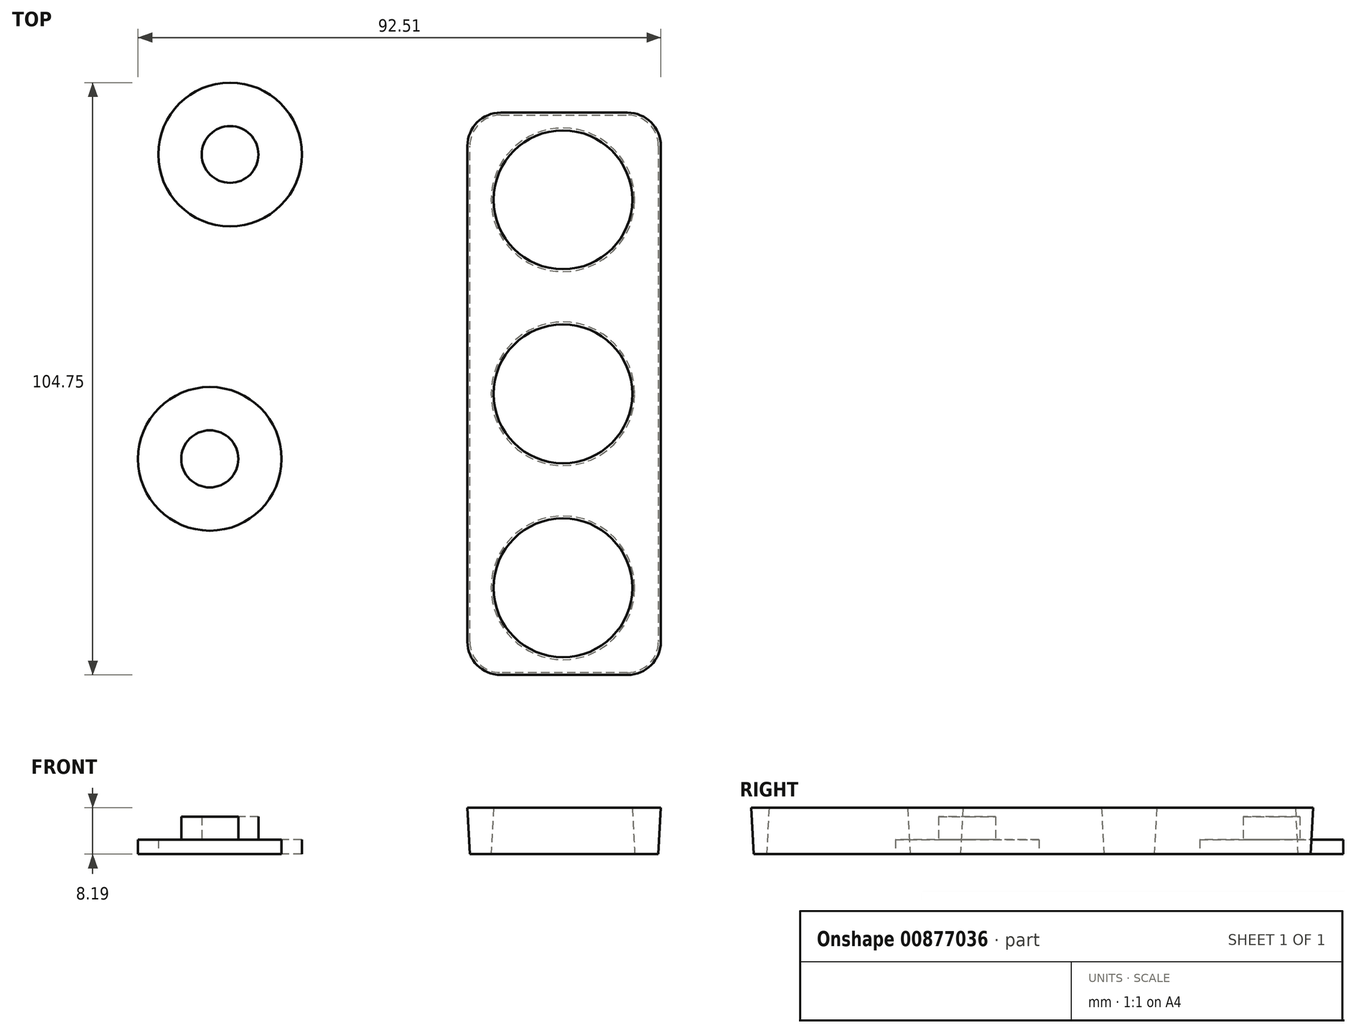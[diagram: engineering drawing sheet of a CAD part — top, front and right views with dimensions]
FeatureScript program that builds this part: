
annotation { "Feature Type Name" : "Feature", "Feature Type Description" : "" }
export const myFeature = defineFeature(function(context is Context, id is Id, definition is map)
    precondition{}
    {
        {
            var Q0;
            Q0=qCreatedBy(makeId("Top.planeOp"),FACE);
            var sketch = newSketch(context, id + "F0", { "sketchPlane" : qUnion([Q0])});
            skCircle(sketch, "E0", {"center": v(0, 0) * mm, "radius": 12.7 * mm});
            skCircle(sketch, "E1", {"center": v(0, 34.3) * mm, "radius": 12.7 * mm});
            skCircle(sketch, "E2.MirrorC", {"center": v(0, -34.3) * mm, "radius": 12.7 * mm});
            skLineSegment(sketch, "E3", {"start": v(-16.47, 21.22) * mm, "end": v(-16.47, -21.22) * mm});
            skLineSegment(sketch, "E4", {"start": v(16.89, 21.22) * mm, "end": v(16.89, -21.22) * mm});
            skLineSegment(sketch, "E5.MirrorCS", {"start": v(-16.47, -21.22) * mm, "end": v(-16.47, 21.22) * mm});
            skLineSegment(sketch, "E6.MirrorCS", {"start": v(16.89, -21.22) * mm, "end": v(16.89, 21.22) * mm});
            skLineSegment(sketch, "E7", {"start": v(-16.47, 21.22) * mm, "end": v(-16.47, 43.83) * mm});
            skLineSegment(sketch, "E8", {"start": v(16.89, 21.22) * mm, "end": v(16.89, 43.83) * mm});
            skLineSegment(sketch, "E9", {"start": v(11.43, 49.3) * mm, "end": v(-11, 49.3) * mm});
            skLineSegment(sketch, "E10", {"start": v(-16.47, -21.22) * mm, "end": v(-16.47, -43.83) * mm});
            skLineSegment(sketch, "E11", {"start": v(-11, -49.3) * mm, "end": v(11.43, -49.3) * mm});
            skLineSegment(sketch, "E12", {"start": v(16.89, -43.83) * mm, "end": v(16.89, -21.22) * mm});
            skPoint(sketch, "E13.visualSharp", {"position": v(-16.47, 49.3) * mm});
            skArc(sketch, "E13.filletArc", {"start": v(-11, 49.3) * mm, "mid": v(-14.87, 47.7) * mm, "end": v(-16.47, 43.83) * mm});
            skPoint(sketch, "E14.visualSharp", {"position": v(16.89, 49.3) * mm});
            skArc(sketch, "E14.filletArc", {"start": v(16.89, 43.83) * mm, "mid": v(15.29, 47.7) * mm, "end": v(11.43, 49.3) * mm});
            skPoint(sketch, "E15.visualSharp", {"position": v(-16.47, -49.3) * mm});
            skArc(sketch, "E15.filletArc", {"start": v(-16.47, -43.83) * mm, "mid": v(-14.87, -47.7) * mm, "end": v(-11, -49.3) * mm});
            skPoint(sketch, "E16.visualSharp", {"position": v(16.89, -49.3) * mm});
            skArc(sketch, "E16.filletArc", {"start": v(11.43, -49.3) * mm, "mid": v(15.29, -47.7) * mm, "end": v(16.89, -43.83) * mm});
            skSolve(sketch);
        }
        {
            var Q0;
            Q0=makeQuery(id+"F0.imprint","IMPRINT",FACE,{"disambiguationData":[TD([[makeQuery(id+"F0.imprint","IMPRINT",EDGE,{"derivedFrom":sQuery(id+"F0.wireOp",EDGE,"E1")}),-1.0]])]});
            extrude(context, id + "F1", {"entities" : qUnion([Q0]), "depth" : 8.2 * mm, "offsetDistance" : 25.4 * mm, "hasDraft" : true, "draftAngle" : 3 * degree});
        }
        {
            var Q0;
            Q0=qCreatedBy(makeId("Top.planeOp"),FACE);
            var sketch = newSketch(context, id + "F2", { "sketchPlane" : qUnion([Q0])});
            skCircle(sketch, "E17", {"center": v(-62.49, -11.5) * mm, "radius": 12.7 * mm});
            skCircle(sketch, "E18", {"center": v(-58.9, 42.33) * mm, "radius": 12.7 * mm});
            skSolve(sketch);
        }
        {
            var Q0;
            Q0 = qSketchRegion(id + "F2", true);
            extrude(context, id + "F3", {"entities" : qUnion([Q0]), "depth" : 2.54 * mm, "offsetDistance" : 25.4 * mm});
        }
        {
            var Q0;
            Q0=makeQuery(id+"F3.opExtrude","CAP_FACE",FACE,{"disambiguationData":[OSD([sQuery(id+"F2.wireOp",EDGE,"E17")])],"isStart":false});
            var sketch = newSketch(context, id + "F4", { "sketchPlane" : qUnion([Q0])});
            skCircle(sketch, "E19", {"center": v(-62.49, -11.5) * mm, "radius": 5.05 * mm});
            skSolve(sketch);
        }
        {
            var Q0;
            Q0 = qSketchRegion(id + "F4", true);
            extrude(context, id + "F5", {"entities" : qUnion([Q0]), "operationType" : NewBodyOperationType.ADD, "depth" : 4.06 * mm, "offsetDistance" : 25.4 * mm});
        }
        {
            var Q0;
            Q0=makeQuery(id+"F3.opExtrude","CAP_FACE",FACE,{"disambiguationData":[OSD([sQuery(id+"F2.wireOp",EDGE,"E18")])],"isStart":false});
            var sketch = newSketch(context, id + "F6", { "sketchPlane" : qUnion([Q0])});
            skCircle(sketch, "E20", {"center": v(-58.9, 42.33) * mm, "radius": 5.02 * mm});
            skSolve(sketch);
        }
        {
            var Q0;
            Q0 = qSketchRegion(id + "F6", true);
            extrude(context, id + "F7", {"entities" : qUnion([Q0]), "operationType" : NewBodyOperationType.ADD, "depth" : 4.06 * mm, "offsetDistance" : 25.4 * mm});
        }
    });
